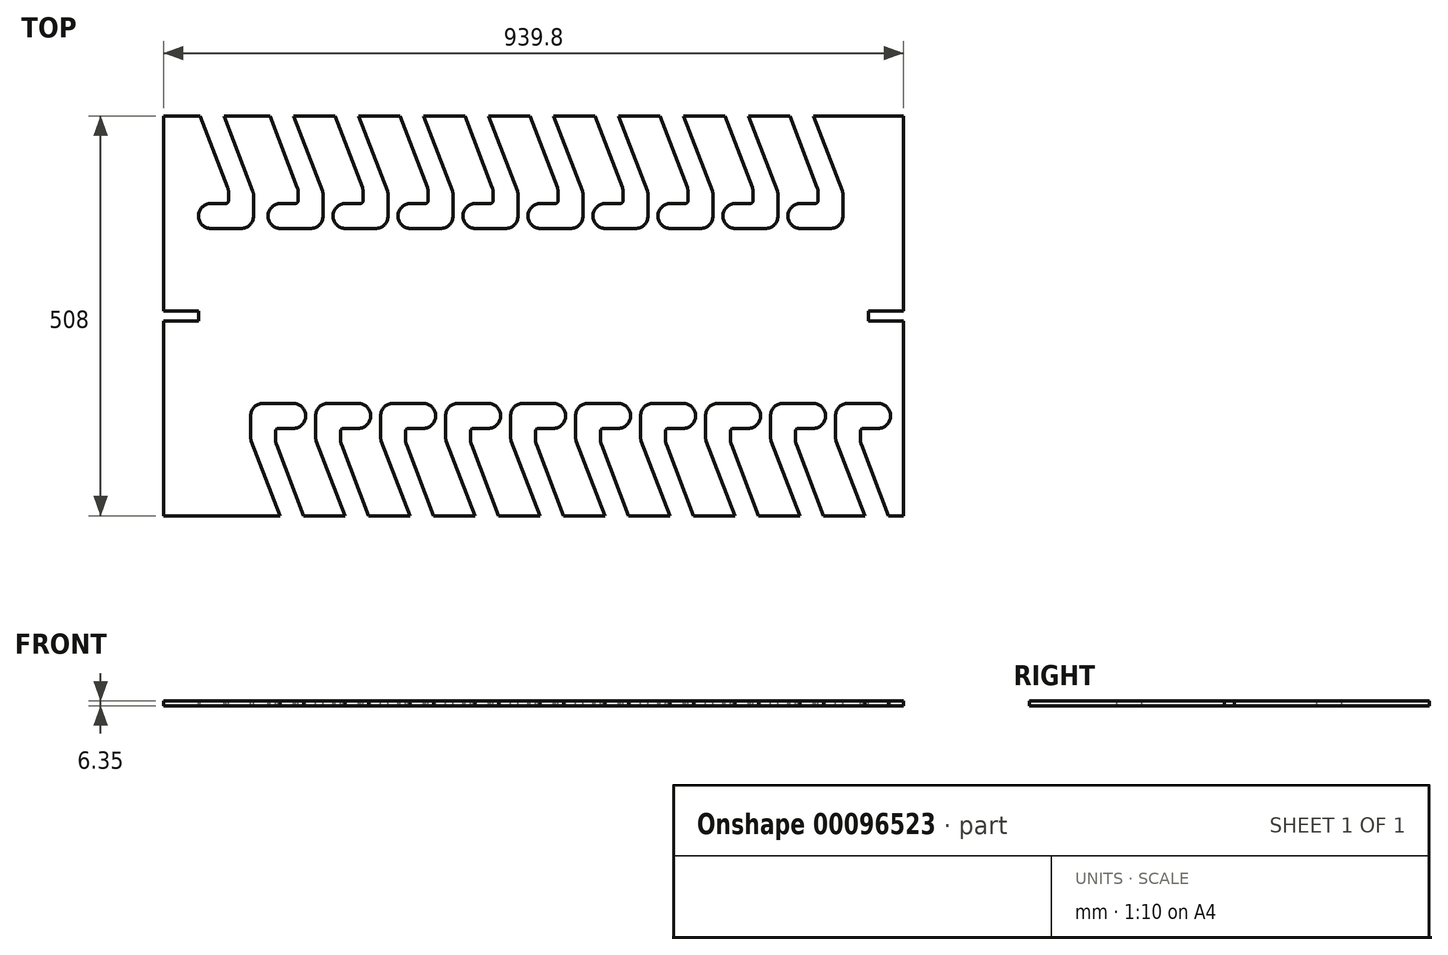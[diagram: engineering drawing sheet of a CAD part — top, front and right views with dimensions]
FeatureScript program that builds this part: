
annotation { "Feature Type Name" : "Feature", "Feature Type Description" : "" }
export const myFeature = defineFeature(function(context is Context, id is Id, definition is map)
    precondition{}
    {
        {
            var Q0;
            Q0=qCreatedBy(makeId("Top.planeOp"),FACE);
            var sketch = newSketch(context, id + "F0", { "sketchPlane" : qUnion([Q0])});
            skLineSegment(sketch, "E0.bottom", {"start": v(0, 0) * mm, "end": v(-939.8, 0) * mm});
            skLineSegment(sketch, "E0.top", {"start": v(0, 508) * mm, "end": v(-939.8, 508) * mm});
            skLineSegment(sketch, "E0.left", {"start": v(0, 0) * mm, "end": v(0, 247.65) * mm});
            skLineSegment(sketch, "E0.right", {"start": v(-939.8, 0) * mm, "end": v(-939.8, 247.65) * mm});
            skLineSegment(sketch, "E1", {"start": v(-939.8, 260.35) * mm, "end": v(-895.35, 260.35) * mm});
            skLineSegment(sketch, "E2", {"start": v(-895.35, 260.35) * mm, "end": v(-895.35, 247.65) * mm});
            skLineSegment(sketch, "E3", {"start": v(-895.35, 247.65) * mm, "end": v(-939.8, 247.65) * mm});
            skLineSegment(sketch, "E4", {"start": v(-939.8, 508) * mm, "end": v(-939.8, 260.35) * mm});
            skLineSegment(sketch, "E5", {"start": v(-939.8, 247.65) * mm, "end": v(-939.8, 0) * mm});
            skLineSegment(sketch, "E6.trimOffspring", {"start": v(-939.8, 260.35) * mm, "end": v(-939.8, 508) * mm});
            skLineSegment(sketch, "E7", {"start": v(0, 260.35) * mm, "end": v(-44.45, 260.35) * mm});
            skLineSegment(sketch, "E8", {"start": v(-44.45, 260.35) * mm, "end": v(-44.45, 247.65) * mm});
            skLineSegment(sketch, "E9", {"start": v(-44.45, 247.65) * mm, "end": v(0, 247.65) * mm});
            skLineSegment(sketch, "E10", {"start": v(0, 260.35) * mm, "end": v(0, 508) * mm});
            skLineSegment(sketch, "E11", {"start": v(0, 247.65) * mm, "end": v(0, 0) * mm});
            skSolve(sketch);
        }
        {
            var Q0;
            Q0=qSketchRegion(id+"F0",true);
            extrude(context, id + "F1", {"entities" : qUnion([Q0]), "oppositeDirection" : true, "depth" : 6.35 * mm});
        }
        {
            var Q0;
            Q0=makeQuery(id+"F1.opExtrude","CAP_FACE",FACE,{"disambiguationData":[OSD([sQuery(id+"F0.wireOp",EDGE,"E0.bottom"),sQuery(id+"F0.wireOp",EDGE,"E0.top"),sQuery(id+"F0.wireOp",EDGE,"E1"),sQuery(id+"F0.wireOp",EDGE,"E2"),sQuery(id+"F0.wireOp",EDGE,"E3"),sQuery(id+"F0.wireOp",EDGE,"E5"),sQuery(id+"F0.wireOp",EDGE,"E6.trimOffspring"),sQuery(id+"F0.wireOp",EDGE,"E7"),sQuery(id+"F0.wireOp",EDGE,"E8"),sQuery(id+"F0.wireOp",EDGE,"E9"),sQuery(id+"F0.wireOp",EDGE,"E11"),sQuery(id+"F0.wireOp",EDGE,"E10")])],"isStart":true});
            var sketch = newSketch(context, id + "F2", { "sketchPlane" : qUnion([Q0])});
            skLineSegment(sketch, "E12", {"start": v(-774.7, 508) * mm, "end": v(-738.14, 412.75) * mm});
            skArc(sketch, "E13", {"start": v(-737.3, 408.2) * mm, "mid": v(-737.5, 410.51) * mm, "end": v(-738.14, 412.75) * mm});
            skLineSegment(sketch, "E14", {"start": v(-737.3, 408.2) * mm, "end": v(-737.3, 380.96) * mm});
            skArc(sketch, "E15", {"start": v(-753.17, 365.08) * mm, "mid": v(-741.94, 369.73) * mm, "end": v(-737.3, 380.96) * mm});
            skLineSegment(sketch, "E16", {"start": v(-753.17, 365.08) * mm, "end": v(-791.27, 365.08) * mm});
            skArc(sketch, "E17", {"start": v(-791.27, 396.83) * mm, "mid": v(-807.14, 380.96) * mm, "end": v(-791.27, 365.08) * mm});
            skLineSegment(sketch, "E18", {"start": v(-791.27, 396.83) * mm, "end": v(-772.22, 396.83) * mm});
            skArc(sketch, "E19", {"start": v(-772.33, 396.83) * mm, "mid": v(-770.05, 397.74) * mm, "end": v(-769.1, 400) * mm});
            skLineSegment(sketch, "E20", {"start": v(-769.1, 400) * mm, "end": v(-769.1, 412.7) * mm});
            skArc(sketch, "E21", {"start": v(-769.1, 412.7) * mm, "mid": v(-769.31, 415.02) * mm, "end": v(-769.94, 417.26) * mm});
            skLineSegment(sketch, "E22", {"start": v(-804.78, 508) * mm, "end": v(-769.94, 417.26) * mm});
            skPoint(sketch, "E23.orphan", {"position": v(-768.21, 412.75) * mm});
            skLineSegment(sketch, "E24", {"start": v(-692.15, 508) * mm, "end": v(-655.59, 412.75) * mm});
            skArc(sketch, "E25", {"start": v(-654.74, 408.2) * mm, "mid": v(-654.96, 410.51) * mm, "end": v(-655.59, 412.75) * mm});
            skLineSegment(sketch, "E26", {"start": v(-654.74, 408.2) * mm, "end": v(-654.74, 380.96) * mm});
            skArc(sketch, "E27", {"start": v(-670.62, 365.08) * mm, "mid": v(-659.4, 369.73) * mm, "end": v(-654.74, 380.96) * mm});
            skLineSegment(sketch, "E28", {"start": v(-670.62, 365.08) * mm, "end": v(-708.72, 365.08) * mm});
            skArc(sketch, "E29", {"start": v(-708.72, 396.83) * mm, "mid": v(-724.6, 380.96) * mm, "end": v(-708.72, 365.08) * mm});
            skLineSegment(sketch, "E30", {"start": v(-708.72, 396.83) * mm, "end": v(-689.67, 396.83) * mm});
            skArc(sketch, "E31", {"start": v(-689.78, 396.83) * mm, "mid": v(-687.5, 397.74) * mm, "end": v(-686.55, 400) * mm});
            skLineSegment(sketch, "E32", {"start": v(-686.55, 400) * mm, "end": v(-686.55, 412.7) * mm});
            skArc(sketch, "E33", {"start": v(-686.55, 412.7) * mm, "mid": v(-686.76, 415.02) * mm, "end": v(-687.4, 417.26) * mm});
            skLineSegment(sketch, "E34", {"start": v(-722.23, 508) * mm, "end": v(-687.4, 417.26) * mm});
            skPoint(sketch, "E35.orphan", {"position": v(-685.66, 412.75) * mm});
            skLineSegment(sketch, "E36", {"start": v(-857.25, 508) * mm, "end": v(-774.7, 508) * mm});
            skLineSegment(sketch, "E37", {"start": v(-774.7, 508) * mm, "end": v(-692.15, 508) * mm});
            skLineSegment(sketch, "E38", {"start": v(-609.6, 508) * mm, "end": v(-573.04, 412.75) * mm});
            skArc(sketch, "E39", {"start": v(-572.2, 408.2) * mm, "mid": v(-572.4, 410.51) * mm, "end": v(-573.04, 412.75) * mm});
            skLineSegment(sketch, "E40", {"start": v(-572.2, 408.2) * mm, "end": v(-572.2, 380.96) * mm});
            skArc(sketch, "E41", {"start": v(-588.07, 365.08) * mm, "mid": v(-576.84, 369.73) * mm, "end": v(-572.2, 380.96) * mm});
            skLineSegment(sketch, "E42", {"start": v(-588.07, 365.08) * mm, "end": v(-626.17, 365.08) * mm});
            skArc(sketch, "E43", {"start": v(-626.17, 396.83) * mm, "mid": v(-642.04, 380.96) * mm, "end": v(-626.17, 365.08) * mm});
            skLineSegment(sketch, "E44", {"start": v(-626.17, 396.83) * mm, "end": v(-607.12, 396.83) * mm});
            skArc(sketch, "E45", {"start": v(-607.23, 396.83) * mm, "mid": v(-604.95, 397.74) * mm, "end": v(-604, 400) * mm});
            skLineSegment(sketch, "E46", {"start": v(-604, 400) * mm, "end": v(-604, 412.7) * mm});
            skArc(sketch, "E47", {"start": v(-604, 412.7) * mm, "mid": v(-604.21, 415.02) * mm, "end": v(-604.84, 417.26) * mm});
            skLineSegment(sketch, "E48", {"start": v(-639.68, 508) * mm, "end": v(-604.84, 417.26) * mm});
            skPoint(sketch, "E49.orphan", {"position": v(-603.11, 412.75) * mm});
            skLineSegment(sketch, "E50", {"start": v(-527.05, 508) * mm, "end": v(-490.49, 412.75) * mm});
            skArc(sketch, "E51", {"start": v(-489.64, 408.2) * mm, "mid": v(-489.86, 410.51) * mm, "end": v(-490.49, 412.75) * mm});
            skLineSegment(sketch, "E52", {"start": v(-489.64, 408.2) * mm, "end": v(-489.64, 380.96) * mm});
            skArc(sketch, "E53", {"start": v(-505.52, 365.08) * mm, "mid": v(-494.3, 369.73) * mm, "end": v(-489.64, 380.96) * mm});
            skLineSegment(sketch, "E54", {"start": v(-505.52, 365.08) * mm, "end": v(-543.62, 365.08) * mm});
            skArc(sketch, "E55", {"start": v(-543.62, 396.83) * mm, "mid": v(-559.5, 380.96) * mm, "end": v(-543.62, 365.08) * mm});
            skLineSegment(sketch, "E56", {"start": v(-543.62, 396.83) * mm, "end": v(-524.57, 396.83) * mm});
            skArc(sketch, "E57", {"start": v(-524.68, 396.83) * mm, "mid": v(-522.4, 397.74) * mm, "end": v(-521.45, 400) * mm});
            skLineSegment(sketch, "E58", {"start": v(-521.45, 400) * mm, "end": v(-521.45, 412.7) * mm});
            skArc(sketch, "E59", {"start": v(-521.45, 412.7) * mm, "mid": v(-521.66, 415.02) * mm, "end": v(-522.3, 417.26) * mm});
            skLineSegment(sketch, "E60", {"start": v(-557.13, 508) * mm, "end": v(-522.3, 417.26) * mm});
            skPoint(sketch, "E61.orphan", {"position": v(-520.56, 412.75) * mm});
            skLineSegment(sketch, "E62", {"start": v(-692.15, 508) * mm, "end": v(-609.6, 508) * mm});
            skLineSegment(sketch, "E63", {"start": v(-609.6, 508) * mm, "end": v(-527.05, 508) * mm});
            skLineSegment(sketch, "E64", {"start": v(-444.5, 508) * mm, "end": v(-407.94, 412.75) * mm});
            skArc(sketch, "E65", {"start": v(-407.1, 408.2) * mm, "mid": v(-407.3, 410.51) * mm, "end": v(-407.94, 412.75) * mm});
            skLineSegment(sketch, "E66", {"start": v(-407.1, 408.2) * mm, "end": v(-407.1, 380.96) * mm});
            skArc(sketch, "E67", {"start": v(-422.97, 365.08) * mm, "mid": v(-411.74, 369.73) * mm, "end": v(-407.1, 380.96) * mm});
            skLineSegment(sketch, "E68", {"start": v(-422.97, 365.08) * mm, "end": v(-461.07, 365.08) * mm});
            skArc(sketch, "E69", {"start": v(-461.07, 396.83) * mm, "mid": v(-476.94, 380.96) * mm, "end": v(-461.07, 365.08) * mm});
            skLineSegment(sketch, "E70", {"start": v(-461.07, 396.83) * mm, "end": v(-442.02, 396.83) * mm});
            skArc(sketch, "E71", {"start": v(-442.13, 396.83) * mm, "mid": v(-439.85, 397.74) * mm, "end": v(-438.9, 400) * mm});
            skLineSegment(sketch, "E72", {"start": v(-438.9, 400) * mm, "end": v(-438.9, 412.7) * mm});
            skArc(sketch, "E73", {"start": v(-438.9, 412.7) * mm, "mid": v(-439.11, 415.02) * mm, "end": v(-439.74, 417.26) * mm});
            skLineSegment(sketch, "E74", {"start": v(-474.58, 508) * mm, "end": v(-439.74, 417.26) * mm});
            skPoint(sketch, "E75.orphan", {"position": v(-438.01, 412.75) * mm});
            skLineSegment(sketch, "E76", {"start": v(-361.95, 508) * mm, "end": v(-325.39, 412.75) * mm});
            skArc(sketch, "E77", {"start": v(-324.54, 408.2) * mm, "mid": v(-324.76, 410.51) * mm, "end": v(-325.39, 412.75) * mm});
            skLineSegment(sketch, "E78", {"start": v(-324.54, 408.2) * mm, "end": v(-324.54, 380.96) * mm});
            skArc(sketch, "E79", {"start": v(-340.42, 365.08) * mm, "mid": v(-329.2, 369.73) * mm, "end": v(-324.54, 380.96) * mm});
            skLineSegment(sketch, "E80", {"start": v(-340.42, 365.08) * mm, "end": v(-378.52, 365.08) * mm});
            skArc(sketch, "E81", {"start": v(-378.52, 396.83) * mm, "mid": v(-394.4, 380.96) * mm, "end": v(-378.52, 365.08) * mm});
            skLineSegment(sketch, "E82", {"start": v(-378.52, 396.83) * mm, "end": v(-359.47, 396.83) * mm});
            skArc(sketch, "E83", {"start": v(-359.58, 396.83) * mm, "mid": v(-357.3, 397.74) * mm, "end": v(-356.35, 400) * mm});
            skLineSegment(sketch, "E84", {"start": v(-356.35, 400) * mm, "end": v(-356.35, 412.7) * mm});
            skArc(sketch, "E85", {"start": v(-356.35, 412.7) * mm, "mid": v(-356.56, 415.02) * mm, "end": v(-357.2, 417.26) * mm});
            skLineSegment(sketch, "E86", {"start": v(-392.03, 508) * mm, "end": v(-357.2, 417.26) * mm});
            skPoint(sketch, "E87.orphan", {"position": v(-355.46, 412.75) * mm});
            skLineSegment(sketch, "E88", {"start": v(-527.05, 508) * mm, "end": v(-444.5, 508) * mm});
            skLineSegment(sketch, "E89", {"start": v(-444.5, 508) * mm, "end": v(-361.95, 508) * mm});
            skLineSegment(sketch, "E90", {"start": v(-279.4, 508) * mm, "end": v(-242.84, 412.75) * mm});
            skArc(sketch, "E91", {"start": v(-242, 408.2) * mm, "mid": v(-242.2, 410.51) * mm, "end": v(-242.84, 412.75) * mm});
            skLineSegment(sketch, "E92", {"start": v(-242, 408.2) * mm, "end": v(-242, 380.96) * mm});
            skArc(sketch, "E93", {"start": v(-257.87, 365.08) * mm, "mid": v(-246.64, 369.73) * mm, "end": v(-242, 380.96) * mm});
            skLineSegment(sketch, "E94", {"start": v(-257.87, 365.08) * mm, "end": v(-295.97, 365.08) * mm});
            skArc(sketch, "E95", {"start": v(-295.97, 396.83) * mm, "mid": v(-311.84, 380.96) * mm, "end": v(-295.97, 365.08) * mm});
            skLineSegment(sketch, "E96", {"start": v(-295.97, 396.83) * mm, "end": v(-276.92, 396.83) * mm});
            skArc(sketch, "E97", {"start": v(-277.03, 396.83) * mm, "mid": v(-274.75, 397.74) * mm, "end": v(-273.8, 400) * mm});
            skLineSegment(sketch, "E98", {"start": v(-273.8, 400) * mm, "end": v(-273.8, 412.7) * mm});
            skArc(sketch, "E99", {"start": v(-273.8, 412.7) * mm, "mid": v(-274.01, 415.02) * mm, "end": v(-274.64, 417.26) * mm});
            skLineSegment(sketch, "E100", {"start": v(-309.48, 508) * mm, "end": v(-274.64, 417.26) * mm});
            skPoint(sketch, "E101.orphan", {"position": v(-272.91, 412.75) * mm});
            skLineSegment(sketch, "E102", {"start": v(-196.85, 508) * mm, "end": v(-160.29, 412.75) * mm});
            skArc(sketch, "E103", {"start": v(-159.44, 408.2) * mm, "mid": v(-159.66, 410.51) * mm, "end": v(-160.29, 412.75) * mm});
            skLineSegment(sketch, "E104", {"start": v(-159.44, 408.2) * mm, "end": v(-159.44, 380.96) * mm});
            skArc(sketch, "E105", {"start": v(-175.32, 365.08) * mm, "mid": v(-164.1, 369.73) * mm, "end": v(-159.44, 380.96) * mm});
            skLineSegment(sketch, "E106", {"start": v(-175.32, 365.08) * mm, "end": v(-213.42, 365.08) * mm});
            skArc(sketch, "E107", {"start": v(-213.42, 396.83) * mm, "mid": v(-229.3, 380.96) * mm, "end": v(-213.42, 365.08) * mm});
            skLineSegment(sketch, "E108", {"start": v(-213.42, 396.83) * mm, "end": v(-194.37, 396.83) * mm});
            skArc(sketch, "E109", {"start": v(-194.48, 396.83) * mm, "mid": v(-192.2, 397.74) * mm, "end": v(-191.25, 400) * mm});
            skLineSegment(sketch, "E110", {"start": v(-191.25, 400) * mm, "end": v(-191.25, 412.7) * mm});
            skArc(sketch, "E111", {"start": v(-191.25, 412.7) * mm, "mid": v(-191.46, 415.02) * mm, "end": v(-192.1, 417.26) * mm});
            skLineSegment(sketch, "E112", {"start": v(-226.93, 508) * mm, "end": v(-192.1, 417.26) * mm});
            skPoint(sketch, "E113.orphan", {"position": v(-190.36, 412.75) * mm});
            skLineSegment(sketch, "E114", {"start": v(-361.95, 508) * mm, "end": v(-279.4, 508) * mm});
            skLineSegment(sketch, "E115", {"start": v(-279.4, 508) * mm, "end": v(-196.85, 508) * mm});
            skLineSegment(sketch, "E116", {"start": v(-114.3, 508) * mm, "end": v(-77.74, 412.75) * mm});
            skArc(sketch, "E117", {"start": v(-76.9, 408.2) * mm, "mid": v(-77.1, 410.51) * mm, "end": v(-77.74, 412.75) * mm});
            skLineSegment(sketch, "E118", {"start": v(-76.9, 408.2) * mm, "end": v(-76.9, 380.96) * mm});
            skArc(sketch, "E119", {"start": v(-92.77, 365.08) * mm, "mid": v(-81.54, 369.73) * mm, "end": v(-76.9, 380.96) * mm});
            skLineSegment(sketch, "E120", {"start": v(-92.77, 365.08) * mm, "end": v(-130.87, 365.08) * mm});
            skArc(sketch, "E121", {"start": v(-130.87, 396.83) * mm, "mid": v(-146.74, 380.96) * mm, "end": v(-130.87, 365.08) * mm});
            skLineSegment(sketch, "E122", {"start": v(-130.87, 396.83) * mm, "end": v(-111.82, 396.83) * mm});
            skArc(sketch, "E123", {"start": v(-111.93, 396.83) * mm, "mid": v(-109.65, 397.74) * mm, "end": v(-108.7, 400) * mm});
            skLineSegment(sketch, "E124", {"start": v(-108.7, 400) * mm, "end": v(-108.7, 412.7) * mm});
            skArc(sketch, "E125", {"start": v(-108.7, 412.7) * mm, "mid": v(-108.91, 415.02) * mm, "end": v(-109.54, 417.26) * mm});
            skLineSegment(sketch, "E126", {"start": v(-144.38, 508) * mm, "end": v(-109.54, 417.26) * mm});
            skPoint(sketch, "E127.orphan", {"position": v(-107.81, 412.75) * mm});
            skLineSegment(sketch, "E128", {"start": v(-196.85, 508) * mm, "end": v(-114.3, 508) * mm});
            skLineSegment(sketch, "E129.MirrorCS", {"start": v(-54.49, 108) * mm, "end": v(-54.49, 95.3) * mm});
            skArc(sketch, "E130.MirrorCS", {"start": v(-54.49, 95.3) * mm, "mid": v(-54.28, 92.98) * mm, "end": v(-53.64, 90.74) * mm});
            skArc(sketch, "E131.MirrorCS", {"start": v(-51.37, 111.17) * mm, "mid": v(-53.58, 110.22) * mm, "end": v(-54.49, 108) * mm});
            skLineSegment(sketch, "E132.MirrorCS", {"start": v(-32.32, 111.17) * mm, "end": v(-51.37, 111.17) * mm});
            skArc(sketch, "E133.MirrorCS", {"start": v(-86.3, 99.8) * mm, "mid": v(-86.08, 97.49) * mm, "end": v(-85.45, 95.25) * mm});
            skLineSegment(sketch, "E134.MirrorCS", {"start": v(-48.89, 0) * mm, "end": v(-85.45, 95.25) * mm});
            skArc(sketch, "E135.MirrorCS", {"start": v(-32.32, 111.17) * mm, "mid": v(-16.45, 127.04) * mm, "end": v(-32.32, 142.92) * mm});
            skLineSegment(sketch, "E136.MirrorCS", {"start": v(-70.42, 142.92) * mm, "end": v(-32.32, 142.92) * mm});
            skLineSegment(sketch, "E137.MirrorCS", {"start": v(-86.3, 99.8) * mm, "end": v(-86.3, 127.04) * mm});
            skLineSegment(sketch, "E138.MirrorCS", {"start": v(-18.81, 0) * mm, "end": v(-53.64, 90.74) * mm});
            skArc(sketch, "E139.MirrorCS", {"start": v(-70.42, 142.92) * mm, "mid": v(-81.65, 138.27) * mm, "end": v(-86.3, 127.04) * mm});
            skPoint(sketch, "E140.MirrorP", {"position": v(107.81, 95.25) * mm});
            skLineSegment(sketch, "E141", {"start": v(-18.81, 0) * mm, "end": v(0, 0) * mm});
            skLineSegment(sketch, "E142.MirrorCS", {"start": v(-137.04, 108) * mm, "end": v(-137.04, 95.3) * mm});
            skArc(sketch, "E143.MirrorCS", {"start": v(-137.04, 95.3) * mm, "mid": v(-136.83, 92.98) * mm, "end": v(-136.2, 90.74) * mm});
            skArc(sketch, "E144.MirrorCS", {"start": v(-133.92, 111.17) * mm, "mid": v(-136.13, 110.22) * mm, "end": v(-137.04, 108) * mm});
            skLineSegment(sketch, "E145.MirrorCS", {"start": v(-114.87, 111.17) * mm, "end": v(-133.92, 111.17) * mm});
            skArc(sketch, "E146.MirrorCS", {"start": v(-168.85, 99.8) * mm, "mid": v(-168.63, 97.49) * mm, "end": v(-168, 95.25) * mm});
            skLineSegment(sketch, "E147.MirrorCS", {"start": v(-131.44, 0) * mm, "end": v(-168, 95.25) * mm});
            skArc(sketch, "E148.MirrorCS", {"start": v(-114.87, 111.17) * mm, "mid": v(-99, 127.04) * mm, "end": v(-114.87, 142.92) * mm});
            skLineSegment(sketch, "E149.MirrorCS", {"start": v(-152.97, 142.92) * mm, "end": v(-114.87, 142.92) * mm});
            skLineSegment(sketch, "E150.MirrorCS", {"start": v(-168.85, 99.8) * mm, "end": v(-168.85, 127.04) * mm});
            skLineSegment(sketch, "E151.MirrorCS", {"start": v(-101.36, 0) * mm, "end": v(-136.2, 90.74) * mm});
            skArc(sketch, "E152.MirrorCS", {"start": v(-152.97, 142.92) * mm, "mid": v(-164.2, 138.27) * mm, "end": v(-168.85, 127.04) * mm});
            skLineSegment(sketch, "E153.MirrorCS", {"start": v(-219.59, 108) * mm, "end": v(-219.59, 95.3) * mm});
            skArc(sketch, "E154.MirrorCS", {"start": v(-219.59, 95.3) * mm, "mid": v(-219.38, 92.98) * mm, "end": v(-218.74, 90.74) * mm});
            skArc(sketch, "E155.MirrorCS", {"start": v(-216.36, 111.17) * mm, "mid": v(-218.64, 110.26) * mm, "end": v(-219.59, 108) * mm});
            skLineSegment(sketch, "E156.MirrorCS", {"start": v(-197.42, 111.17) * mm, "end": v(-216.47, 111.17) * mm});
            skArc(sketch, "E157.MirrorCS", {"start": v(-251.4, 99.8) * mm, "mid": v(-251.18, 97.49) * mm, "end": v(-250.55, 95.25) * mm});
            skLineSegment(sketch, "E158.MirrorCS", {"start": v(-213.99, 0) * mm, "end": v(-250.55, 95.25) * mm});
            skArc(sketch, "E159.MirrorCS", {"start": v(-197.42, 111.17) * mm, "mid": v(-181.55, 127.04) * mm, "end": v(-197.42, 142.92) * mm});
            skLineSegment(sketch, "E160.MirrorCS", {"start": v(-235.52, 142.92) * mm, "end": v(-197.42, 142.92) * mm});
            skLineSegment(sketch, "E161.MirrorCS", {"start": v(-251.4, 99.8) * mm, "end": v(-251.4, 127.04) * mm});
            skLineSegment(sketch, "E162.MirrorCS", {"start": v(-183.91, 0) * mm, "end": v(-218.74, 90.74) * mm});
            skArc(sketch, "E163.MirrorCS", {"start": v(-235.52, 142.92) * mm, "mid": v(-246.75, 138.27) * mm, "end": v(-251.4, 127.04) * mm});
            skLineSegment(sketch, "E164.MirrorCS", {"start": v(-302.14, 108) * mm, "end": v(-302.14, 95.3) * mm});
            skArc(sketch, "E165.MirrorCS", {"start": v(-302.14, 95.3) * mm, "mid": v(-301.93, 92.98) * mm, "end": v(-301.3, 90.74) * mm});
            skArc(sketch, "E166.MirrorCS", {"start": v(-299.02, 111.17) * mm, "mid": v(-301.23, 110.22) * mm, "end": v(-302.14, 108) * mm});
            skLineSegment(sketch, "E167.MirrorCS", {"start": v(-279.97, 111.17) * mm, "end": v(-299.02, 111.17) * mm});
            skArc(sketch, "E168.MirrorCS", {"start": v(-333.95, 99.8) * mm, "mid": v(-333.73, 97.49) * mm, "end": v(-333.1, 95.25) * mm});
            skLineSegment(sketch, "E169.MirrorCS", {"start": v(-296.54, 0) * mm, "end": v(-333.1, 95.25) * mm});
            skArc(sketch, "E170.MirrorCS", {"start": v(-279.97, 111.17) * mm, "mid": v(-264.1, 127.04) * mm, "end": v(-279.97, 142.92) * mm});
            skLineSegment(sketch, "E171.MirrorCS", {"start": v(-318.07, 142.92) * mm, "end": v(-279.97, 142.92) * mm});
            skLineSegment(sketch, "E172.MirrorCS", {"start": v(-333.95, 99.8) * mm, "end": v(-333.95, 127.04) * mm});
            skLineSegment(sketch, "E173.MirrorCS", {"start": v(-266.46, 0) * mm, "end": v(-301.3, 90.74) * mm});
            skArc(sketch, "E174.MirrorCS", {"start": v(-318.07, 142.92) * mm, "mid": v(-329.3, 138.27) * mm, "end": v(-333.95, 127.04) * mm});
            skLineSegment(sketch, "E175.MirrorCS", {"start": v(-384.69, 108) * mm, "end": v(-384.69, 95.3) * mm});
            skArc(sketch, "E176.MirrorCS", {"start": v(-384.69, 95.3) * mm, "mid": v(-384.48, 92.98) * mm, "end": v(-383.84, 90.74) * mm});
            skArc(sketch, "E177.MirrorCS", {"start": v(-381.57, 111.17) * mm, "mid": v(-383.78, 110.22) * mm, "end": v(-384.69, 108) * mm});
            skLineSegment(sketch, "E178.MirrorCS", {"start": v(-362.52, 111.17) * mm, "end": v(-381.57, 111.17) * mm});
            skArc(sketch, "E179.MirrorCS", {"start": v(-416.5, 99.8) * mm, "mid": v(-416.28, 97.49) * mm, "end": v(-415.65, 95.25) * mm});
            skLineSegment(sketch, "E180.MirrorCS", {"start": v(-379.09, 0) * mm, "end": v(-415.65, 95.25) * mm});
            skArc(sketch, "E181.MirrorCS", {"start": v(-362.52, 111.17) * mm, "mid": v(-346.65, 127.04) * mm, "end": v(-362.52, 142.92) * mm});
            skLineSegment(sketch, "E182.MirrorCS", {"start": v(-400.62, 142.92) * mm, "end": v(-362.52, 142.92) * mm});
            skLineSegment(sketch, "E183.MirrorCS", {"start": v(-416.5, 99.8) * mm, "end": v(-416.5, 127.04) * mm});
            skLineSegment(sketch, "E184.MirrorCS", {"start": v(-349.01, 0) * mm, "end": v(-383.84, 90.74) * mm});
            skArc(sketch, "E185.MirrorCS", {"start": v(-400.62, 142.92) * mm, "mid": v(-411.85, 138.27) * mm, "end": v(-416.5, 127.04) * mm});
            skLineSegment(sketch, "E186", {"start": v(-349.01, 0) * mm, "end": v(-298.21, 0) * mm});
            skLineSegment(sketch, "E187.MirrorCS", {"start": v(-467.24, 108) * mm, "end": v(-467.24, 95.3) * mm});
            skArc(sketch, "E188.MirrorCS", {"start": v(-467.24, 95.3) * mm, "mid": v(-467.03, 92.98) * mm, "end": v(-466.4, 90.74) * mm});
            skArc(sketch, "E189.MirrorCS", {"start": v(-464.12, 111.17) * mm, "mid": v(-466.33, 110.22) * mm, "end": v(-467.24, 108) * mm});
            skLineSegment(sketch, "E190.MirrorCS", {"start": v(-445.07, 111.17) * mm, "end": v(-464.12, 111.17) * mm});
            skArc(sketch, "E191.MirrorCS", {"start": v(-499.05, 99.8) * mm, "mid": v(-498.83, 97.49) * mm, "end": v(-498.2, 95.25) * mm});
            skLineSegment(sketch, "E192.MirrorCS", {"start": v(-461.64, 0) * mm, "end": v(-498.2, 95.25) * mm});
            skArc(sketch, "E193.MirrorCS", {"start": v(-445.07, 111.17) * mm, "mid": v(-429.2, 127.04) * mm, "end": v(-445.07, 142.92) * mm});
            skLineSegment(sketch, "E194.MirrorCS", {"start": v(-483.17, 142.92) * mm, "end": v(-445.07, 142.92) * mm});
            skLineSegment(sketch, "E195.MirrorCS", {"start": v(-499.05, 99.8) * mm, "end": v(-499.05, 127.04) * mm});
            skLineSegment(sketch, "E196.MirrorCS", {"start": v(-431.56, 0) * mm, "end": v(-466.4, 90.74) * mm});
            skArc(sketch, "E197.MirrorCS", {"start": v(-483.17, 142.92) * mm, "mid": v(-494.4, 138.27) * mm, "end": v(-499.05, 127.04) * mm});
            skLineSegment(sketch, "E198.MirrorCS", {"start": v(-549.79, 108) * mm, "end": v(-549.79, 95.3) * mm});
            skArc(sketch, "E199.MirrorCS", {"start": v(-549.79, 95.3) * mm, "mid": v(-549.58, 92.98) * mm, "end": v(-548.94, 90.74) * mm});
            skArc(sketch, "E200.MirrorCS", {"start": v(-546.67, 111.17) * mm, "mid": v(-548.88, 110.22) * mm, "end": v(-549.79, 108) * mm});
            skLineSegment(sketch, "E201.MirrorCS", {"start": v(-527.62, 111.17) * mm, "end": v(-546.67, 111.17) * mm});
            skArc(sketch, "E202.MirrorCS", {"start": v(-581.6, 99.8) * mm, "mid": v(-581.38, 97.49) * mm, "end": v(-580.75, 95.25) * mm});
            skLineSegment(sketch, "E203.MirrorCS", {"start": v(-544.19, 0) * mm, "end": v(-580.75, 95.25) * mm});
            skArc(sketch, "E204.MirrorCS", {"start": v(-527.62, 111.17) * mm, "mid": v(-511.75, 127.04) * mm, "end": v(-527.62, 142.92) * mm});
            skLineSegment(sketch, "E205.MirrorCS", {"start": v(-565.72, 142.92) * mm, "end": v(-527.62, 142.92) * mm});
            skLineSegment(sketch, "E206.MirrorCS", {"start": v(-581.6, 99.8) * mm, "end": v(-581.6, 127.04) * mm});
            skLineSegment(sketch, "E207.MirrorCS", {"start": v(-514.11, 0) * mm, "end": v(-548.94, 90.74) * mm});
            skArc(sketch, "E208.MirrorCS", {"start": v(-565.72, 142.92) * mm, "mid": v(-576.95, 138.27) * mm, "end": v(-581.6, 127.04) * mm});
            skLineSegment(sketch, "E209.MirrorCS", {"start": v(-632.34, 108) * mm, "end": v(-632.34, 95.3) * mm});
            skArc(sketch, "E210.MirrorCS", {"start": v(-632.34, 95.3) * mm, "mid": v(-632.13, 92.98) * mm, "end": v(-631.5, 90.74) * mm});
            skArc(sketch, "E211.MirrorCS", {"start": v(-629.22, 111.17) * mm, "mid": v(-631.43, 110.22) * mm, "end": v(-632.34, 108) * mm});
            skLineSegment(sketch, "E212.MirrorCS", {"start": v(-610.17, 111.17) * mm, "end": v(-629.22, 111.17) * mm});
            skArc(sketch, "E213.MirrorCS", {"start": v(-664.15, 99.8) * mm, "mid": v(-663.93, 97.49) * mm, "end": v(-663.3, 95.25) * mm});
            skLineSegment(sketch, "E214.MirrorCS", {"start": v(-626.74, 0) * mm, "end": v(-663.3, 95.25) * mm});
            skArc(sketch, "E215.MirrorCS", {"start": v(-610.17, 111.17) * mm, "mid": v(-594.3, 127.04) * mm, "end": v(-610.17, 142.92) * mm});
            skLineSegment(sketch, "E216.MirrorCS", {"start": v(-648.27, 142.92) * mm, "end": v(-610.17, 142.92) * mm});
            skLineSegment(sketch, "E217.MirrorCS", {"start": v(-664.15, 99.8) * mm, "end": v(-664.15, 127.04) * mm});
            skLineSegment(sketch, "E218.MirrorCS", {"start": v(-596.66, 0) * mm, "end": v(-631.5, 90.74) * mm});
            skArc(sketch, "E219.MirrorCS", {"start": v(-648.27, 142.92) * mm, "mid": v(-659.5, 138.27) * mm, "end": v(-664.15, 127.04) * mm});
            skLineSegment(sketch, "E220.MirrorCS", {"start": v(-714.89, 108) * mm, "end": v(-714.89, 95.3) * mm});
            skArc(sketch, "E221.MirrorCS", {"start": v(-714.89, 95.3) * mm, "mid": v(-714.68, 92.98) * mm, "end": v(-714.04, 90.74) * mm});
            skArc(sketch, "E222.MirrorCS", {"start": v(-711.77, 111.17) * mm, "mid": v(-713.98, 110.22) * mm, "end": v(-714.89, 108) * mm});
            skLineSegment(sketch, "E223.MirrorCS", {"start": v(-692.72, 111.17) * mm, "end": v(-711.77, 111.17) * mm});
            skArc(sketch, "E224.MirrorCS", {"start": v(-746.7, 99.8) * mm, "mid": v(-746.48, 97.49) * mm, "end": v(-745.85, 95.25) * mm});
            skLineSegment(sketch, "E225.MirrorCS", {"start": v(-709.29, 0) * mm, "end": v(-745.85, 95.25) * mm});
            skArc(sketch, "E226.MirrorCS", {"start": v(-692.72, 111.17) * mm, "mid": v(-676.85, 127.04) * mm, "end": v(-692.72, 142.92) * mm});
            skLineSegment(sketch, "E227.MirrorCS", {"start": v(-730.82, 142.92) * mm, "end": v(-692.72, 142.92) * mm});
            skLineSegment(sketch, "E228.MirrorCS", {"start": v(-746.7, 99.8) * mm, "end": v(-746.7, 127.04) * mm});
            skLineSegment(sketch, "E229.MirrorCS", {"start": v(-679.21, 0) * mm, "end": v(-714.04, 90.74) * mm});
            skArc(sketch, "E230.MirrorCS", {"start": v(-730.82, 142.92) * mm, "mid": v(-742.05, 138.27) * mm, "end": v(-746.7, 127.04) * mm});
            skLineSegment(sketch, "E231.MirrorCS", {"start": v(-797.44, 108) * mm, "end": v(-797.44, 95.3) * mm});
            skArc(sketch, "E232.MirrorCS", {"start": v(-797.44, 95.3) * mm, "mid": v(-797.23, 92.98) * mm, "end": v(-796.6, 90.74) * mm});
            skArc(sketch, "E233.MirrorCS", {"start": v(-794.32, 111.17) * mm, "mid": v(-796.53, 110.22) * mm, "end": v(-797.44, 108) * mm});
            skLineSegment(sketch, "E234.MirrorCS", {"start": v(-775.27, 111.17) * mm, "end": v(-794.32, 111.17) * mm});
            skArc(sketch, "E235.MirrorCS", {"start": v(-829.25, 99.8) * mm, "mid": v(-829.03, 97.49) * mm, "end": v(-828.4, 95.25) * mm});
            skLineSegment(sketch, "E236.MirrorCS", {"start": v(-791.84, 0) * mm, "end": v(-828.4, 95.25) * mm});
            skArc(sketch, "E237.MirrorCS", {"start": v(-775.27, 111.17) * mm, "mid": v(-759.4, 127.04) * mm, "end": v(-775.27, 142.92) * mm});
            skLineSegment(sketch, "E238.MirrorCS", {"start": v(-813.37, 142.92) * mm, "end": v(-775.27, 142.92) * mm});
            skLineSegment(sketch, "E239.MirrorCS", {"start": v(-829.25, 99.8) * mm, "end": v(-829.25, 127.04) * mm});
            skLineSegment(sketch, "E240.MirrorCS", {"start": v(-761.76, 0) * mm, "end": v(-796.6, 90.74) * mm});
            skArc(sketch, "E241.MirrorCS", {"start": v(-813.37, 142.92) * mm, "mid": v(-824.6, 138.27) * mm, "end": v(-829.25, 127.04) * mm});
            skLineSegment(sketch, "E242", {"start": v(-48.89, 0) * mm, "end": v(-101.36, 0) * mm});
            skLineSegment(sketch, "E243", {"start": v(-131.44, 0) * mm, "end": v(-183.91, 0) * mm});
            skLineSegment(sketch, "E244", {"start": v(-213.99, 0) * mm, "end": v(-266.46, 0) * mm});
            skLineSegment(sketch, "E245", {"start": v(-379.09, 0) * mm, "end": v(-431.56, 0) * mm});
            skLineSegment(sketch, "E246", {"start": v(-461.64, 0) * mm, "end": v(-514.11, 0) * mm});
            skLineSegment(sketch, "E247", {"start": v(-544.19, 0) * mm, "end": v(-596.66, 0) * mm});
            skLineSegment(sketch, "E248", {"start": v(-626.74, 0) * mm, "end": v(-679.21, 0) * mm});
            skLineSegment(sketch, "E249", {"start": v(-709.29, 0) * mm, "end": v(-761.76, 0) * mm});
            skLineSegment(sketch, "E250", {"start": v(-791.84, 0) * mm, "end": v(-939.8, 0) * mm});
            skLineSegment(sketch, "E251.0", {"start": v(-863.12, 508) * mm, "end": v(-828.3, 417.26) * mm});
            skLineSegment(sketch, "E252", {"start": v(-863.12, 508) * mm, "end": v(-826.56, 412.75) * mm});
            skArc(sketch, "E253", {"start": v(-825.72, 408.2) * mm, "mid": v(-825.93, 410.51) * mm, "end": v(-826.56, 412.75) * mm});
            skLineSegment(sketch, "E254", {"start": v(-825.72, 408.2) * mm, "end": v(-825.72, 380.96) * mm});
            skArc(sketch, "E255", {"start": v(-841.6, 365.08) * mm, "mid": v(-830.37, 369.73) * mm, "end": v(-825.72, 380.96) * mm});
            skLineSegment(sketch, "E256", {"start": v(-841.6, 365.08) * mm, "end": v(-879.7, 365.08) * mm});
            skArc(sketch, "E257", {"start": v(-879.7, 396.83) * mm, "mid": v(-895.57, 380.96) * mm, "end": v(-879.7, 365.08) * mm});
            skLineSegment(sketch, "E258", {"start": v(-879.7, 396.83) * mm, "end": v(-860.64, 396.83) * mm});
            skArc(sketch, "E259", {"start": v(-860.76, 396.83) * mm, "mid": v(-858.47, 397.74) * mm, "end": v(-857.52, 400) * mm});
            skLineSegment(sketch, "E260", {"start": v(-857.52, 400) * mm, "end": v(-857.52, 412.7) * mm});
            skArc(sketch, "E261", {"start": v(-857.52, 412.7) * mm, "mid": v(-857.74, 415.02) * mm, "end": v(-858.37, 417.26) * mm});
            skLineSegment(sketch, "E262", {"start": v(-893.2, 508) * mm, "end": v(-858.37, 417.26) * mm});
            skPoint(sketch, "E263.orphan", {"position": v(-856.64, 412.75) * mm});
            skLineSegment(sketch, "E264", {"start": v(-893.2, 508) * mm, "end": v(-114.3, 508) * mm});
            skSolve(sketch);
        }
        {
            var Q0;
            Q0=qSketchRegion(id+"F2",true);
            var Q1;
            Q1=makeQuery(id+"F2.imprint","IMPRINT",FACE,{"disambiguationData":[TD([[makeQuery(id+"F2.imprint","IMPRINT",EDGE,{"derivedFrom":sQuery(id+"F2.wireOp",EDGE,"E231.MirrorCS")}),-1.0]])]});
            var Q2;
            Q2=makeQuery(id+"F2.imprint","IMPRINT",FACE,{"disambiguationData":[TD([[makeQuery(id+"F2.imprint","IMPRINT",EDGE,{"derivedFrom":sQuery(id+"F2.wireOp",EDGE,"E220.MirrorCS")}),-1.0]])]});
            var Q3;
            Q3=makeQuery(id+"F2.imprint","IMPRINT",FACE,{"disambiguationData":[TD([[makeQuery(id+"F2.imprint","IMPRINT",EDGE,{"derivedFrom":sQuery(id+"F2.wireOp",EDGE,"E209.MirrorCS")}),-1.0]])]});
            var Q4;
            Q4=makeQuery(id+"F2.imprint","IMPRINT",FACE,{"disambiguationData":[TD([[makeQuery(id+"F2.imprint","IMPRINT",EDGE,{"derivedFrom":sQuery(id+"F2.wireOp",EDGE,"E198.MirrorCS")}),-1.0]])]});
            var Q5;
            Q5=makeQuery(id+"F2.imprint","IMPRINT",FACE,{"disambiguationData":[TD([[makeQuery(id+"F2.imprint","IMPRINT",EDGE,{"derivedFrom":sQuery(id+"F2.wireOp",EDGE,"E187.MirrorCS")}),-1.0]])]});
            var Q6;
            Q6=makeQuery(id+"F2.imprint","IMPRINT",FACE,{"disambiguationData":[TD([[makeQuery(id+"F2.imprint","IMPRINT",EDGE,{"derivedFrom":sQuery(id+"F2.wireOp",EDGE,"E175.MirrorCS")}),-1.0]])]});
            var Q7;
            Q7=makeQuery(id+"F2.imprint","IMPRINT",FACE,{"disambiguationData":[TD([[makeQuery(id+"F2.imprint","IMPRINT",EDGE,{"derivedFrom":sQuery(id+"F2.wireOp",EDGE,"E164.MirrorCS")}),-1.0]])]});
            var Q8;
            {var subQ6=sQuery(id+"F2.wireOp",EDGE,"E153.MirrorCS");Q8=makeQuery(id+"F2.imprint","IMPRINT",FACE,{"disambiguationData":[TD([[makeQuery(id+"F2.imprint","IMPRINT",EDGE,{"derivedFrom":subQ6}),-1.0]])]});}
            var Q9;
            Q9=makeQuery(id+"F2.imprint","IMPRINT",FACE,{"disambiguationData":[TD([[makeQuery(id+"F2.imprint","IMPRINT",EDGE,{"derivedFrom":sQuery(id+"F2.wireOp",EDGE,"E142.MirrorCS")}),-1.0]])]});
            var Q10;
            Q10=makeQuery(id+"F2.imprint","IMPRINT",FACE,{"disambiguationData":[TD([[makeQuery(id+"F2.imprint","IMPRINT",EDGE,{"derivedFrom":sQuery(id+"F2.wireOp",EDGE,"E129.MirrorCS")}),-1.0]])]});
            extrude(context, id + "F3", {"entities" : qUnion([Q0, Q1, Q2, Q3, Q4, Q5, Q6, Q7, Q8, Q9, Q10]), "operationType" : NewBodyOperationType.REMOVE, "oppositeDirection" : true, "depth" : 25.4 * mm});
        }
    });
